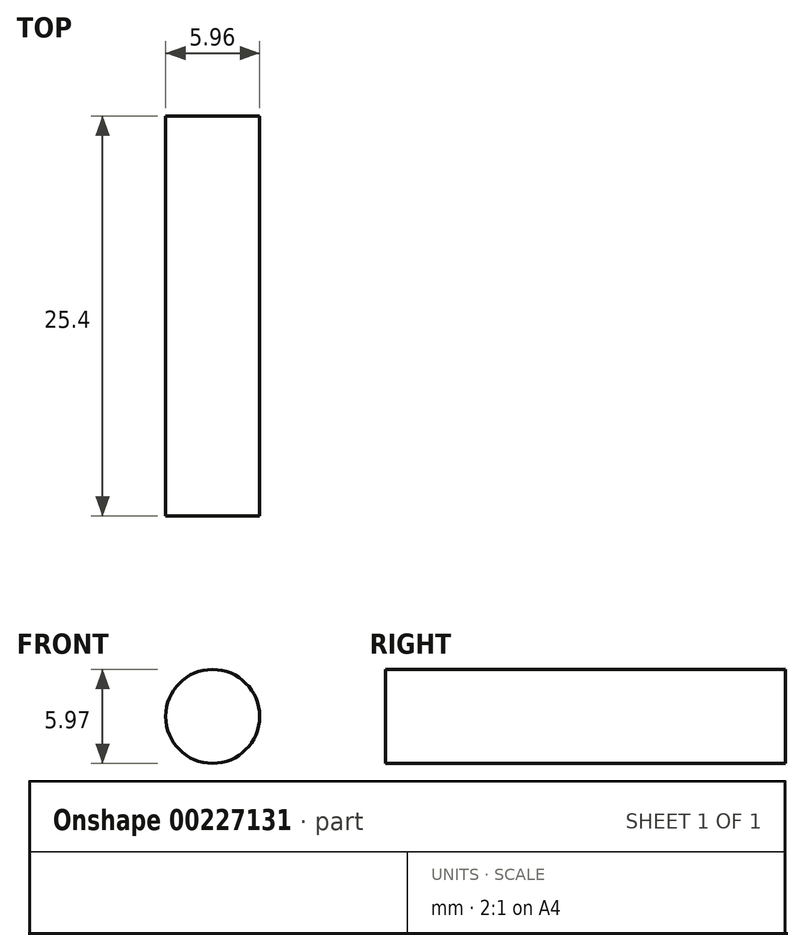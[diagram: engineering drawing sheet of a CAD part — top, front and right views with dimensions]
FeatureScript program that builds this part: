
annotation { "Feature Type Name" : "Feature", "Feature Type Description" : "" }
export const myFeature = defineFeature(function(context is Context, id is Id, definition is map)
    precondition{}
    {
        {
            var Q0;
            Q0=qCreatedBy(makeId("Front.planeOp"),FACE);
            var sketch = newSketch(context, id + "F0", { "sketchPlane" : qUnion([Q0])});
            skLineSegment(sketch, "E0", {"start": v(-34.4, 0) * mm, "end": v(0, 0) * mm, "construction": true});
            skLineSegment(sketch, "E1", {"start": v(0, 0) * mm, "end": v(0, 65.34) * mm});
            skLineSegment(sketch, "E2.MirrorCS", {"start": v(34.4, 0) * mm, "end": v(0, 0) * mm});
            skLineSegment(sketch, "E3.MirrorCS", {"start": v(0, 0) * mm, "end": v(0, -65.34) * mm, "construction": true});
            skFitSpline(sketch, "E4", {"points": [v(0, 65.34) * mm, v(0, 0) * mm, v(-34.4, 0) * mm, v(-34.8, 2.41) * mm, v(-0.5, 65.38) * mm, v(0, 65.34) * mm], "construction": true});
            skFitSpline(sketch, "E5", {"points": [v(0, 65.34) * mm, v(0, 0) * mm, v(34.4, 0) * mm, v(34.7, 1.85) * mm, v(0.15, 65.36) * mm, v(0, 65.34) * mm]});
            skFitSpline(sketch, "E6", {"points": [v(0, -65.34) * mm, v(-2.46, -65.17) * mm, v(-34.92, -2.23) * mm, v(-34.4, 0) * mm, v(0, 0) * mm, v(0, -65.34) * mm], "construction": true});
            skFitSpline(sketch, "E7", {"points": [v(0, -65.34) * mm, v(0, 0) * mm, v(34.4, 0) * mm, v(35.2, -4.32) * mm, v(3.59, -64.82) * mm, v(0, -65.34) * mm], "construction": true});
            skSolve(sketch);
        }
        {
            var Q0;
            Q0 = qSketchRegion(id + "F0", true);
            extrude(context, id + "F1", {"entities" : qUnion([Q0]), "depth" : 25.4 * mm});
        }
        {
            var Q0;
            Q0=makeQuery(id+"F1.opExtrude","CAP_FACE",FACE,{"disambiguationData":[OSD([sQuery(id+"F0.wireOp",EDGE,"E5")])],"isStart":true});
            var sketch = newSketch(context, id + "F2", { "sketchPlane" : qUnion([Q0])});
            skLineSegment(sketch, "E8", {"start": v(-34.4, 0) * mm, "end": v(3.04, 51.3) * mm});
            skPoint(sketch, "E9", {"position": v(-34.4, 0) * mm});
            skCircle(sketch, "E10", {"center": v(-15.68, 25.65) * mm, "radius": 2.98 * mm});
            skSolve(sketch);
        }
        {
            var Q0;
            {var subQ0=sQuery(id+"F2.wireOp",EDGE,"E10");var subQ1=sQuery(id+"F2.wireOp",EDGE,"E8");var subQ2=makeQuery(id+"F2.imprint","INTERSECT",VERTEX,{"disambiguationData":[OD(0.0)],"derivedFrom":[subQ1,subQ0]});Q0=makeQuery(id+"F2.imprint","IMPRINT",FACE,{"disambiguationData":[TD([[makeQuery(id+"F2.imprint","IMPRINT",EDGE,{"disambiguationData":[TD([[subQ2,-1.0]])],"derivedFrom":subQ1}),1.0]])]});}
            var Q1;
            {var subQ0=sQuery(id+"F2.wireOp",EDGE,"E10");var subQ1=sQuery(id+"F2.wireOp",EDGE,"E8");var subQ2=makeQuery(id+"F2.imprint","INTERSECT",VERTEX,{"disambiguationData":[OD(0.0)],"derivedFrom":[subQ1,subQ0]});Q1=makeQuery(id+"F2.imprint","IMPRINT",FACE,{"disambiguationData":[TD([[makeQuery(id+"F2.imprint","IMPRINT",EDGE,{"disambiguationData":[TD([[subQ2,-1.0]])],"derivedFrom":subQ1}),-1.0]])]});}
            extrude(context, id + "F3", {"entities" : qUnion([Q0, Q1]), "operationType" : NewBodyOperationType.REMOVE, "endBound" : BoundingType.UP_TO_NEXT, "oppositeDirection" : true, "depth" : 25.4 * mm});
        }
    });
